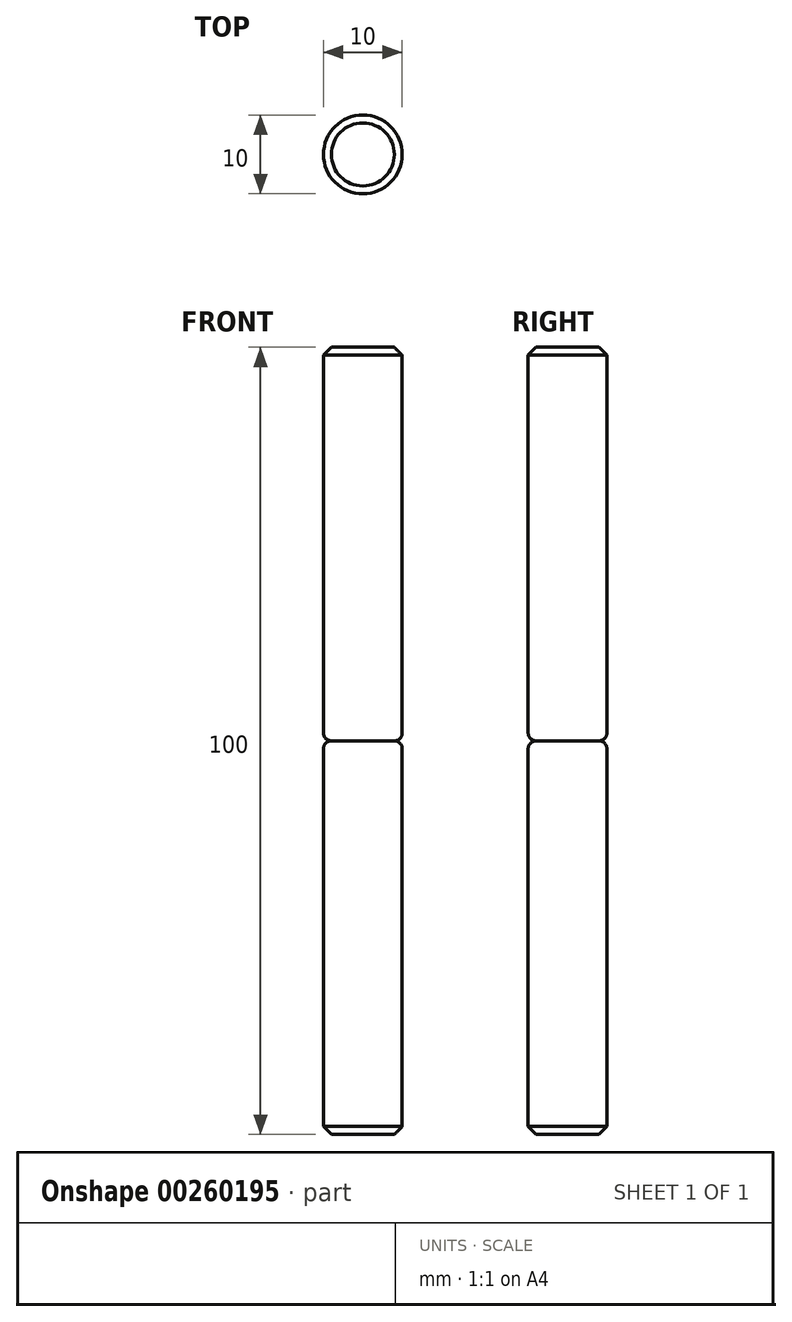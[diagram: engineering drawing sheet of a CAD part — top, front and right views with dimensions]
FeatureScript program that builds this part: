
annotation { "Feature Type Name" : "Feature", "Feature Type Description" : "" }
export const myFeature = defineFeature(function(context is Context, id is Id, definition is map)
    precondition{}
    {
        {
            var Q0;
            Q0=qCreatedBy(makeId("Top.planeOp"),FACE);
            var sketch = newSketch(context, id + "F0", { "sketchPlane" : qUnion([Q0])});
            skCircle(sketch, "E0", {"center": v(0, 0) * mm, "radius": 5 * mm});
            skSolve(sketch);
        }
        {
            var Q0;
            Q0=makeQuery(id+"F0.imprint","IMPRINT",FACE,{"disambiguationData":[TD([[makeQuery(id+"F0.imprint","IMPRINT",EDGE,{"derivedFrom":sQuery(id+"F0.wireOp",EDGE,"E0")}),1.0]])]});
            var Q1;
            Q1=sQuery(id+"F0.wireOp",EDGE,"E0");
            extrude(context, id + "F1", {"entities" : qUnion([Q0]), "surfaceEntities" : qUnion([Q1]), "depth" : 50 * mm});
        }
        {
            var Q0;
            Q0=makeQuery(id+"F1.opExtrude","CAP_EDGE",EDGE,{"disambiguationData":[OSD([sQuery(id+"F0.wireOp",EDGE,"E0")])],"isStart":false});
            fillet(context, id + "F2", {"entities" : qUnion([Q0]), "radius" : 1 * mm, "tangentPropagation" : true, "allowEdgeOverflow" : false});
        }
        {
            var Q0;
            Q0=makeQuery(id+"F1.opExtrude","CAP_EDGE",EDGE,{"disambiguationData":[OSD([sQuery(id+"F0.wireOp",EDGE,"E0")])],"isStart":true});
            chamfer(context, id + "F3", {"entities" : qUnion([Q0]), "width" : 1 * mm, "tangentPropagation" : true});
        }
        {
            var Q0;
            Q0=makeQuery(id+"F1.opExtrude","SWEPT_BODY",BODY,{"disambiguationData":[OSD([sQuery(id+"F0.wireOp",EDGE,"E0")])]});
            var Q1;
            Q1=makeQuery(id+"F1.opExtrude","CAP_FACE",FACE,{"disambiguationData":[OSD([sQuery(id+"F0.wireOp",EDGE,"E0")])],"isStart":false});
            mirror(context, id + "F4", {"operationType" : NewBodyOperationType.ADD, "entities" : qUnion([Q0]), "mirrorPlane" : qUnion([Q1])});
        }
    });
